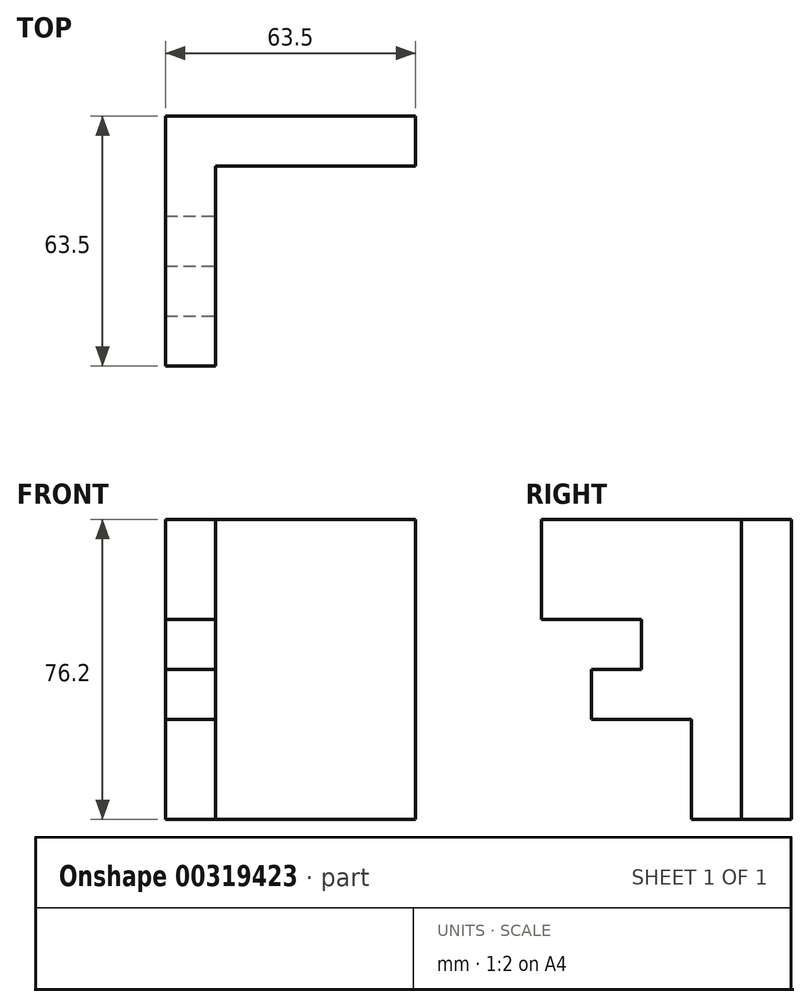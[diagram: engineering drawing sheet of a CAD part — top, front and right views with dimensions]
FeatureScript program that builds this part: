
annotation { "Feature Type Name" : "Feature", "Feature Type Description" : "" }
export const myFeature = defineFeature(function(context is Context, id is Id, definition is map)
    precondition{}
    {
        {
            var Q0;
            Q0=qCreatedBy(makeId("Right.planeOp"),FACE);
            var sketch = newSketch(context, id + "F0", { "sketchPlane" : qUnion([Q0])});
            skLineSegment(sketch, "E0", {"start": v(-38.1, 41.68) * mm, "end": v(25.4, 41.68) * mm});
            skLineSegment(sketch, "E1", {"start": v(25.4, 41.68) * mm, "end": v(25.4, -34.52) * mm});
            skLineSegment(sketch, "E2", {"start": v(25.4, -34.52) * mm, "end": v(0, -34.52) * mm});
            skLineSegment(sketch, "E3", {"start": v(0, -34.52) * mm, "end": v(0, -9.12) * mm});
            skLineSegment(sketch, "E4", {"start": v(-38.1, 16.28) * mm, "end": v(-38.1, 41.68) * mm});
            skLineSegment(sketch, "E5", {"start": v(0, -9.12) * mm, "end": v(-25.4, -9.12) * mm});
            skLineSegment(sketch, "E6", {"start": v(-25.4, -9.12) * mm, "end": v(-25.4, 3.58) * mm});
            skLineSegment(sketch, "E7", {"start": v(-25.4, 3.58) * mm, "end": v(-12.7, 3.58) * mm});
            skLineSegment(sketch, "E8", {"start": v(-12.7, 3.58) * mm, "end": v(-12.7, 16.28) * mm});
            skLineSegment(sketch, "E9", {"start": v(-12.7, 16.28) * mm, "end": v(-38.1, 16.28) * mm});
            skSolve(sketch);
        }
        {
            var Q0;
            Q0=makeQuery(id+"F0.imprint","IMPRINT",FACE,{"disambiguationData":[TD([[makeQuery(id+"F0.imprint","IMPRINT",EDGE,{"derivedFrom":sQuery(id+"F0.wireOp",EDGE,"E0")}),-1.0]])]});
            extrude(context, id + "F1", {"entities" : qUnion([Q0]), "oppositeDirection" : true, "depth" : 12.7 * mm});
        }
        {
            var Q0;
            Q0=makeQuery(id+"F1.opExtrude","SWEPT_FACE",FACE,{"disambiguationData":[OSD([sQuery(id+"F0.wireOp",EDGE,"E1")])]});
            var sketch = newSketch(context, id + "F2", { "sketchPlane" : qUnion([Q0])});
            skLineSegment(sketch, "E10", {"start": v(0, 41.68) * mm, "end": v(-50.8, 41.68) * mm});
            skLineSegment(sketch, "E11", {"start": v(-50.8, 41.68) * mm, "end": v(-50.8, -34.52) * mm});
            skLineSegment(sketch, "E12", {"start": v(-50.8, -34.52) * mm, "end": v(0, -34.52) * mm});
            skSolve(sketch);
        }
        {
            var Q0;
            Q0=makeQuery(id+"F2.imprint","IMPRINT",FACE,{"disambiguationData":[TD([[makeQuery(id+"F2.imprint","IMPRINT",EDGE,{"derivedFrom":sQuery(id+"F2.wireOp",EDGE,"E10")}),1.0]])]});
            extrude(context, id + "F3", {"entities" : qUnion([Q0]), "operationType" : NewBodyOperationType.ADD, "oppositeDirection" : true, "depth" : 12.7 * mm});
        }
    });
